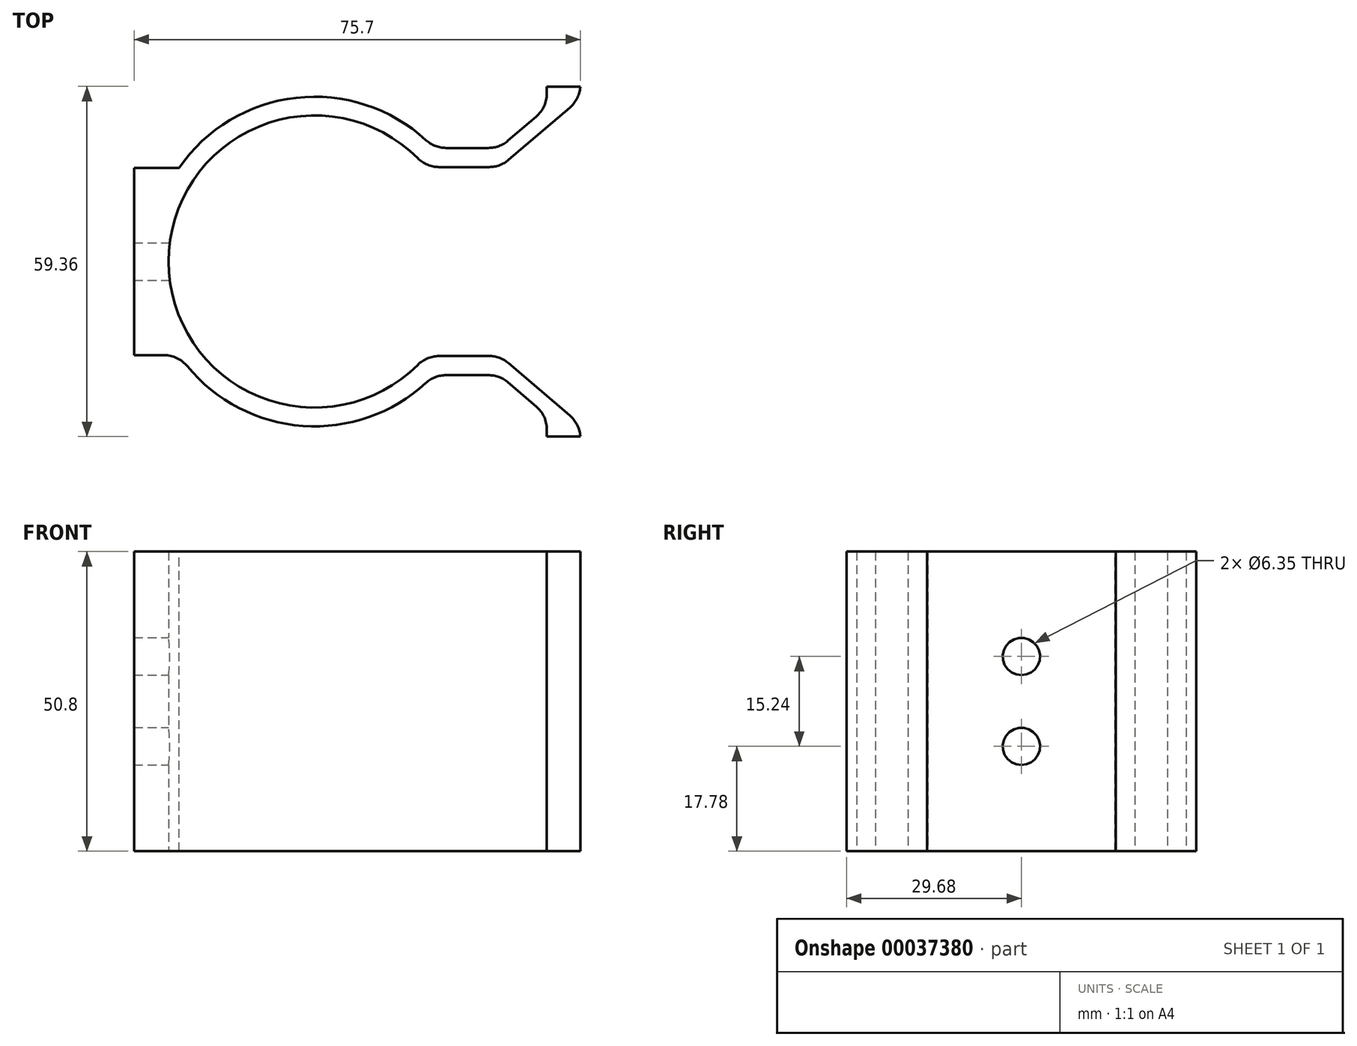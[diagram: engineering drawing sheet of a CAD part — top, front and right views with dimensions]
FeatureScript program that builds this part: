
annotation { "Feature Type Name" : "Feature", "Feature Type Description" : "" }
export const myFeature = defineFeature(function(context is Context, id is Id, definition is map)
    precondition{}
    {
        {
            var Q0;
            Q0=qCreatedBy(makeId("Top.planeOp"),FACE);
            var sketch = newSketch(context, id + "F0", { "sketchPlane" : qUnion([Q0])});
            skCircle(sketch, "E0", {"center": v(0, 0) * mm, "radius": 24.77 * mm});
            skCircle(sketch, "E1", {"center": v(0, 0) * mm, "radius": 27.94 * mm});
            skLineSegment(sketch, "E2", {"start": v(15.57, 19.26) * mm, "end": v(31.37, 19.26) * mm});
            skLineSegment(sketch, "E3", {"start": v(31.37, 19.26) * mm, "end": v(39.4, 26.11) * mm});
            skLineSegment(sketch, "E4", {"start": v(39.4, 26.11) * mm, "end": v(39.4, 29.68) * mm});
            skLineSegment(sketch, "E5", {"start": v(18.88, 16.02) * mm, "end": v(31.48, 16.02) * mm});
            skLineSegment(sketch, "E6", {"start": v(31.48, 16.02) * mm, "end": v(44.8, 27.39) * mm});
            skLineSegment(sketch, "E7", {"start": v(44.8, 27.39) * mm, "end": v(45.09, 29.68) * mm});
            skLineSegment(sketch, "E8", {"start": v(45.09, 29.68) * mm, "end": v(39.4, 29.68) * mm});
            skLineSegment(sketch, "E9", {"start": v(0, 0) * mm, "end": v(11.9, 0) * mm});
            skLineSegment(sketch, "E10.MirrorCS", {"start": v(18.88, -16.02) * mm, "end": v(31.48, -16.02) * mm});
            skLineSegment(sketch, "E11.MirrorCS", {"start": v(15.57, -19.26) * mm, "end": v(31.37, -19.26) * mm});
            skLineSegment(sketch, "E12.MirrorCS", {"start": v(31.48, -16.02) * mm, "end": v(44.8, -27.39) * mm});
            skLineSegment(sketch, "E13.MirrorCS", {"start": v(31.37, -19.26) * mm, "end": v(39.4, -26.11) * mm});
            skLineSegment(sketch, "E14.MirrorCS", {"start": v(44.8, -27.39) * mm, "end": v(45.09, -29.68) * mm});
            skLineSegment(sketch, "E15.MirrorCS", {"start": v(45.09, -29.68) * mm, "end": v(39.4, -29.68) * mm});
            skLineSegment(sketch, "E16.MirrorCS", {"start": v(39.4, -26.11) * mm, "end": v(39.4, -29.68) * mm});
            skSolve(sketch);
        }
        {
            var Q0;
            {var subQ4=sQuery(id+"F0.wireOp",EDGE,"E3");Q0=makeQuery(id+"F0.imprint","IMPRINT",FACE,{"disambiguationData":[TD([[makeQuery(id+"F0.imprint","IMPRINT",EDGE,{"derivedFrom":subQ4}),-1.0]])]});}
            var Q1;
            {var subQ1=sQuery(id+"F0.wireOp",EDGE,"E12.MirrorCS");Q1=makeQuery(id+"F0.imprint","IMPRINT",FACE,{"disambiguationData":[TD([[makeQuery(id+"F0.imprint","IMPRINT",EDGE,{"derivedFrom":subQ1}),-1.0]])]});}
            var Q2;
            {var subQ3=sQuery(id+"F0.wireOp",EDGE,"E0");var subQ5=sQuery(id+"F0.wireOp",EDGE,"E2");var subQ7=makeQuery(id+"F0.imprint","INTERSECT",VERTEX,{"derivedFrom":[subQ3,subQ5]});Q2=makeQuery(id+"F0.imprint","IMPRINT",FACE,{"disambiguationData":[TD([[makeQuery(id+"F0.imprint","IMPRINT",EDGE,{"disambiguationData":[TD([[subQ7,-1.0]])],"derivedFrom":subQ3}),-1.0]])]});}
            var Q3;
            {var subQ3=sQuery(id+"F0.wireOp",EDGE,"E0");var subQ5=sQuery(id+"F0.wireOp",EDGE,"E2");var subQ7=makeQuery(id+"F0.imprint","INTERSECT",VERTEX,{"derivedFrom":[subQ3,subQ5]});Q3=makeQuery(id+"F0.imprint","IMPRINT",FACE,{"disambiguationData":[TD([[makeQuery(id+"F0.imprint","IMPRINT",EDGE,{"disambiguationData":[TD([[subQ7,1.0]])],"derivedFrom":subQ3}),-1.0]])]});}
            var Q4;
            {var subQ3=sQuery(id+"F0.wireOp",EDGE,"E0");var subQ5=sQuery(id+"F0.wireOp",EDGE,"E10.MirrorCS");var subQ7=makeQuery(id+"F0.imprint","INTERSECT",VERTEX,{"derivedFrom":[subQ3,subQ5]});Q4=makeQuery(id+"F0.imprint","IMPRINT",FACE,{"disambiguationData":[TD([[makeQuery(id+"F0.imprint","IMPRINT",EDGE,{"disambiguationData":[TD([[subQ7,1.0]])],"derivedFrom":subQ3}),-1.0]])]});}
            extrude(context, id + "F1", {"entities" : qUnion([Q0, Q1, Q2, Q3, Q4]), "depth" : 50.8 * mm});
        }
        {
            var Q0;
            Q0=qCreatedBy(makeId("Right.planeOp"),FACE);
            var sketch = newSketch(context, id + "F2", { "sketchPlane" : qUnion([Q0])});
            skCircle(sketch, "E17", {"center": v(0, 33.02) * mm, "radius": 3.18 * mm});
            skCircle(sketch, "E18", {"center": v(0, 17.78) * mm, "radius": 3.18 * mm});
            skSolve(sketch);
        }
        {
            var Q0;
            Q0 = qSketchRegion(id + "F2", true);
            extrude(context, id + "F3", {"entities" : qUnion([Q0]), "operationType" : NewBodyOperationType.REMOVE, "oppositeDirection" : true, "depth" : 127 * mm});
        }
        {
            var Q0;
            Q0=makeQuery(id+"F1.opExtrude","CAP_FACE",FACE,{"disambiguationData":[OSD([sQuery(id+"F0.wireOp",EDGE,"E0"),sQuery(id+"F0.wireOp",EDGE,"E1"),sQuery(id+"F0.wireOp",EDGE,"E2"),sQuery(id+"F0.wireOp",EDGE,"E3"),sQuery(id+"F0.wireOp",EDGE,"E4"),sQuery(id+"F0.wireOp",EDGE,"E5"),sQuery(id+"F0.wireOp",EDGE,"E6"),sQuery(id+"F0.wireOp",EDGE,"E7"),sQuery(id+"F0.wireOp",EDGE,"E8"),sQuery(id+"F0.wireOp",EDGE,"E10.MirrorCS"),sQuery(id+"F0.wireOp",EDGE,"E11.MirrorCS"),sQuery(id+"F0.wireOp",EDGE,"E12.MirrorCS"),sQuery(id+"F0.wireOp",EDGE,"E13.MirrorCS"),sQuery(id+"F0.wireOp",EDGE,"E14.MirrorCS"),sQuery(id+"F0.wireOp",EDGE,"E15.MirrorCS"),sQuery(id+"F0.wireOp",EDGE,"E16.MirrorCS")])],"isStart":false});
            var sketch = newSketch(context, id + "F4", { "sketchPlane" : qUnion([Q0])});
            skLineSegment(sketch, "E19", {"start": v(-23, 15.88) * mm, "end": v(-30.61, 15.88) * mm});
            skLineSegment(sketch, "E20", {"start": v(-30.61, 15.88) * mm, "end": v(-30.61, -15.88) * mm});
            skLineSegment(sketch, "E21", {"start": v(-30.61, -15.88) * mm, "end": v(-23, -15.88) * mm});
            skLineSegment(sketch, "E22", {"start": v(-23, -15.88) * mm, "end": v(-26.62, 0) * mm});
            skPoint(sketch, "E22.endSnap0", {"position": v(-24.77, 0) * mm});
            skLineSegment(sketch, "E23", {"start": v(-26.62, 0) * mm, "end": v(-23, 15.88) * mm});
            skSolve(sketch);
        }
        {
            var Q0;
            Q0 = qSketchRegion(id + "F4", true);
            extrude(context, id + "F5", {"entities" : qUnion([Q0]), "operationType" : NewBodyOperationType.ADD, "oppositeDirection" : true, "depth" : 50.8 * mm});
        }
        {
            var Q0;
            Q0 = qSketchRegion(id + "F2", true);
            extrude(context, id + "F6", {"entities" : qUnion([Q0]), "operationType" : NewBodyOperationType.REMOVE, "oppositeDirection" : true, "depth" : 279.4 * mm});
        }
        {
            var Q0;
            Q0=makeQuery(id+"F5.opExtrude","SWEPT_EDGE",EDGE,{"disambiguationData":[OSD([sQuery(id+"F0.wireOp",EDGE,"E1"),sQuery(id+"F4.wireOp",EDGE,"E19"),sQuery(id+"F4.wireOp",EDGE,"E23")])]});
            var Q1;
            Q1=makeQuery(id+"F5.opExtrude","SWEPT_EDGE",EDGE,{"disambiguationData":[OSD([sQuery(id+"F0.wireOp",EDGE,"E1"),sQuery(id+"F4.wireOp",EDGE,"E21"),sQuery(id+"F4.wireOp",EDGE,"E22")])]});
            var Q2;
            Q2=makeQuery(id+"F1.opExtrude","SWEPT_EDGE",EDGE,{"disambiguationData":[OSD([sQuery(id+"F0.wireOp",EDGE,"E1"),sQuery(id+"F0.wireOp",EDGE,"E11.MirrorCS")])]});
            var Q3;
            Q3=makeQuery(id+"F1.opExtrude","SWEPT_EDGE",EDGE,{"disambiguationData":[OSD([sQuery(id+"F0.wireOp",EDGE,"E11.MirrorCS"),sQuery(id+"F0.wireOp",EDGE,"E13.MirrorCS")])]});
            var Q4;
            Q4=makeQuery(id+"F1.opExtrude","SWEPT_EDGE",EDGE,{"disambiguationData":[OSD([sQuery(id+"F0.wireOp",EDGE,"E13.MirrorCS"),sQuery(id+"F0.wireOp",EDGE,"E16.MirrorCS")])]});
            var Q5;
            Q5=makeQuery(id+"F1.opExtrude","SWEPT_EDGE",EDGE,{"disambiguationData":[OSD([sQuery(id+"F0.wireOp",EDGE,"E10.MirrorCS"),sQuery(id+"F0.wireOp",EDGE,"E12.MirrorCS")])]});
            var Q6;
            Q6=makeQuery(id+"F1.opExtrude","SWEPT_EDGE",EDGE,{"disambiguationData":[OSD([sQuery(id+"F0.wireOp",EDGE,"E0"),sQuery(id+"F0.wireOp",EDGE,"E10.MirrorCS")])]});
            var Q7;
            Q7=makeQuery(id+"F1.opExtrude","SWEPT_EDGE",EDGE,{"disambiguationData":[OSD([sQuery(id+"F0.wireOp",EDGE,"E12.MirrorCS"),sQuery(id+"F0.wireOp",EDGE,"E14.MirrorCS")])]});
            var Q8;
            Q8=makeQuery(id+"F1.opExtrude","SWEPT_EDGE",EDGE,{"disambiguationData":[OSD([sQuery(id+"F0.wireOp",EDGE,"E6"),sQuery(id+"F0.wireOp",EDGE,"E7")])]});
            var Q9;
            Q9=makeQuery(id+"F1.opExtrude","SWEPT_EDGE",EDGE,{"disambiguationData":[OSD([sQuery(id+"F0.wireOp",EDGE,"E5"),sQuery(id+"F0.wireOp",EDGE,"E6")])]});
            var Q10;
            Q10=makeQuery(id+"F1.opExtrude","SWEPT_EDGE",EDGE,{"disambiguationData":[OSD([sQuery(id+"F0.wireOp",EDGE,"E2"),sQuery(id+"F0.wireOp",EDGE,"E3")])]});
            var Q11;
            Q11=makeQuery(id+"F1.opExtrude","SWEPT_EDGE",EDGE,{"disambiguationData":[OSD([sQuery(id+"F0.wireOp",EDGE,"E3"),sQuery(id+"F0.wireOp",EDGE,"E4")])]});
            var Q12;
            Q12=makeQuery(id+"F1.opExtrude","SWEPT_EDGE",EDGE,{"disambiguationData":[OSD([sQuery(id+"F0.wireOp",EDGE,"E1"),sQuery(id+"F0.wireOp",EDGE,"E2")])]});
            var Q13;
            Q13=makeQuery(id+"F1.opExtrude","SWEPT_EDGE",EDGE,{"disambiguationData":[OSD([sQuery(id+"F0.wireOp",EDGE,"E0"),sQuery(id+"F0.wireOp",EDGE,"E5")])]});
            fillet(context, id + "F7", {"entities" : qUnion([Q0, Q1, Q2, Q3, Q4, Q5, Q6, Q7, Q8, Q9, Q10, Q11, Q12, Q13]), "radius" : 5.08 * mm, "tangentPropagation" : true, "allowEdgeOverflow" : false});
        }
    });
